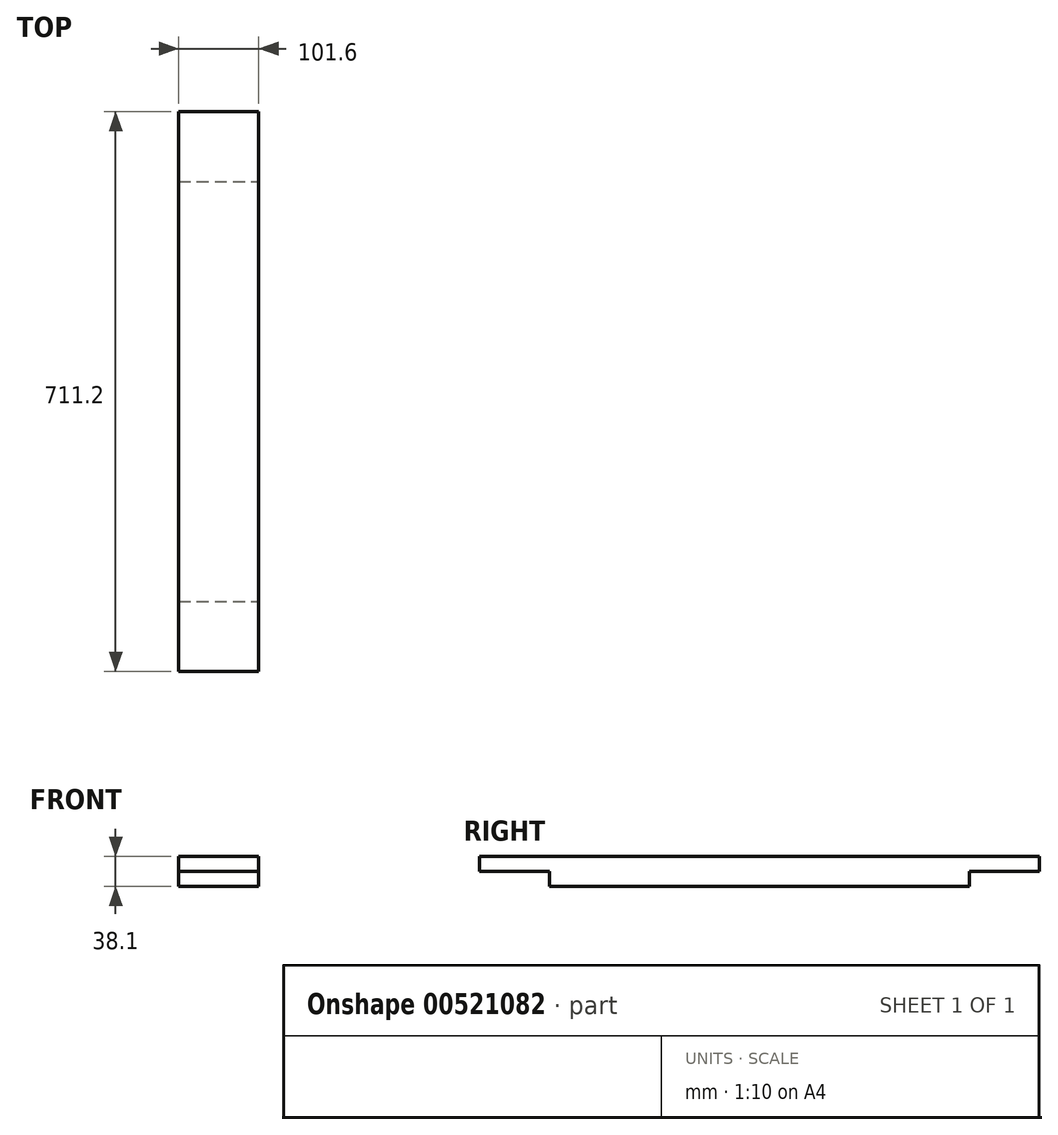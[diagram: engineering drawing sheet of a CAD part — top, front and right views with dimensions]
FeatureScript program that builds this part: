
annotation { "Feature Type Name" : "Feature", "Feature Type Description" : "" }
export const myFeature = defineFeature(function(context is Context, id is Id, definition is map)
    precondition{}
    {
        {
            var Q0;
            Q0=qCreatedBy(makeId("Front.planeOp"),FACE);
            var sketch = newSketch(context, id + "F0", { "sketchPlane" : qUnion([Q0])});
            skLineSegment(sketch, "E0", {"start": v(-68.16, 0) * mm, "end": v(67.52, 0) * mm, "construction": true});
            skLineSegment(sketch, "E1", {"start": v(0, 41.7) * mm, "end": v(0, -39.58) * mm, "construction": true});
            skLineSegment(sketch, "E2.bottom", {"start": v(-50.8, 19.05) * mm, "end": v(50.8, 19.05) * mm});
            skLineSegment(sketch, "E2.top", {"start": v(-50.8, -19.05) * mm, "end": v(50.8, -19.05) * mm});
            skLineSegment(sketch, "E2.left", {"start": v(-50.8, 19.05) * mm, "end": v(-50.8, -19.05) * mm});
            skLineSegment(sketch, "E2.right", {"start": v(50.8, 19.05) * mm, "end": v(50.8, -19.05) * mm});
            skSolve(sketch);
        }
        {
            var Q0;
            Q0 = qSketchRegion(id + "F0", true);
            extrude(context, id + "F1", {"entities" : qUnion([Q0]), "endBound" : BoundingType.SYMMETRIC, "depth" : 711.2 * mm, "offsetDistance" : 25.4 * mm});
        }
        {
            var Q0;
            Q0=makeQuery(id+"F1.opExtrude","SWEPT_FACE",FACE,{"disambiguationData":[OSD([sQuery(id+"F0.wireOp",EDGE,"E2.right")])]});
            var sketch = newSketch(context, id + "F2", { "sketchPlane" : qUnion([Q0])});
            skLineSegment(sketch, "E3.bottom", {"start": v(-355.6, -19.05) * mm, "end": v(-266.7, -19.05) * mm});
            skLineSegment(sketch, "E3.top", {"start": v(-355.6, 0) * mm, "end": v(-266.7, 0) * mm});
            skLineSegment(sketch, "E3.left", {"start": v(-355.6, -19.05) * mm, "end": v(-355.6, 0) * mm});
            skLineSegment(sketch, "E3.right", {"start": v(-266.7, -19.05) * mm, "end": v(-266.7, 0) * mm});
            skLineSegment(sketch, "E4", {"start": v(-355.6, 0) * mm, "end": v(355.6, 0) * mm, "construction": true});
            skLineSegment(sketch, "E5.bottom", {"start": v(355.6, -19.05) * mm, "end": v(266.7, -19.05) * mm});
            skLineSegment(sketch, "E5.top", {"start": v(355.6, 0) * mm, "end": v(266.7, 0) * mm});
            skLineSegment(sketch, "E5.left", {"start": v(355.6, -19.05) * mm, "end": v(355.6, 0) * mm});
            skLineSegment(sketch, "E5.right", {"start": v(266.7, -19.05) * mm, "end": v(266.7, 0) * mm});
            skSolve(sketch);
        }
        {
            var Q0;
            Q0=makeQuery(id+"F2.imprint","IMPRINT",FACE,{"disambiguationData":[TD([[makeQuery(id+"F2.imprint","IMPRINT",EDGE,{"derivedFrom":sQuery(id+"F2.wireOp",EDGE,"E5.bottom")}),1.0]])]});
            var Q1;
            Q1=makeQuery(id+"F2.imprint","IMPRINT",FACE,{"disambiguationData":[TD([[makeQuery(id+"F2.imprint","IMPRINT",EDGE,{"derivedFrom":sQuery(id+"F2.wireOp",EDGE,"E3.bottom")}),1.0]])]});
            extrude(context, id + "F3", {"entities" : qUnion([Q0, Q1]), "operationType" : NewBodyOperationType.REMOVE, "endBound" : BoundingType.THROUGH_ALL, "oppositeDirection" : true, "depth" : 25.4 * mm, "offsetDistance" : 25.4 * mm});
        }
    });
